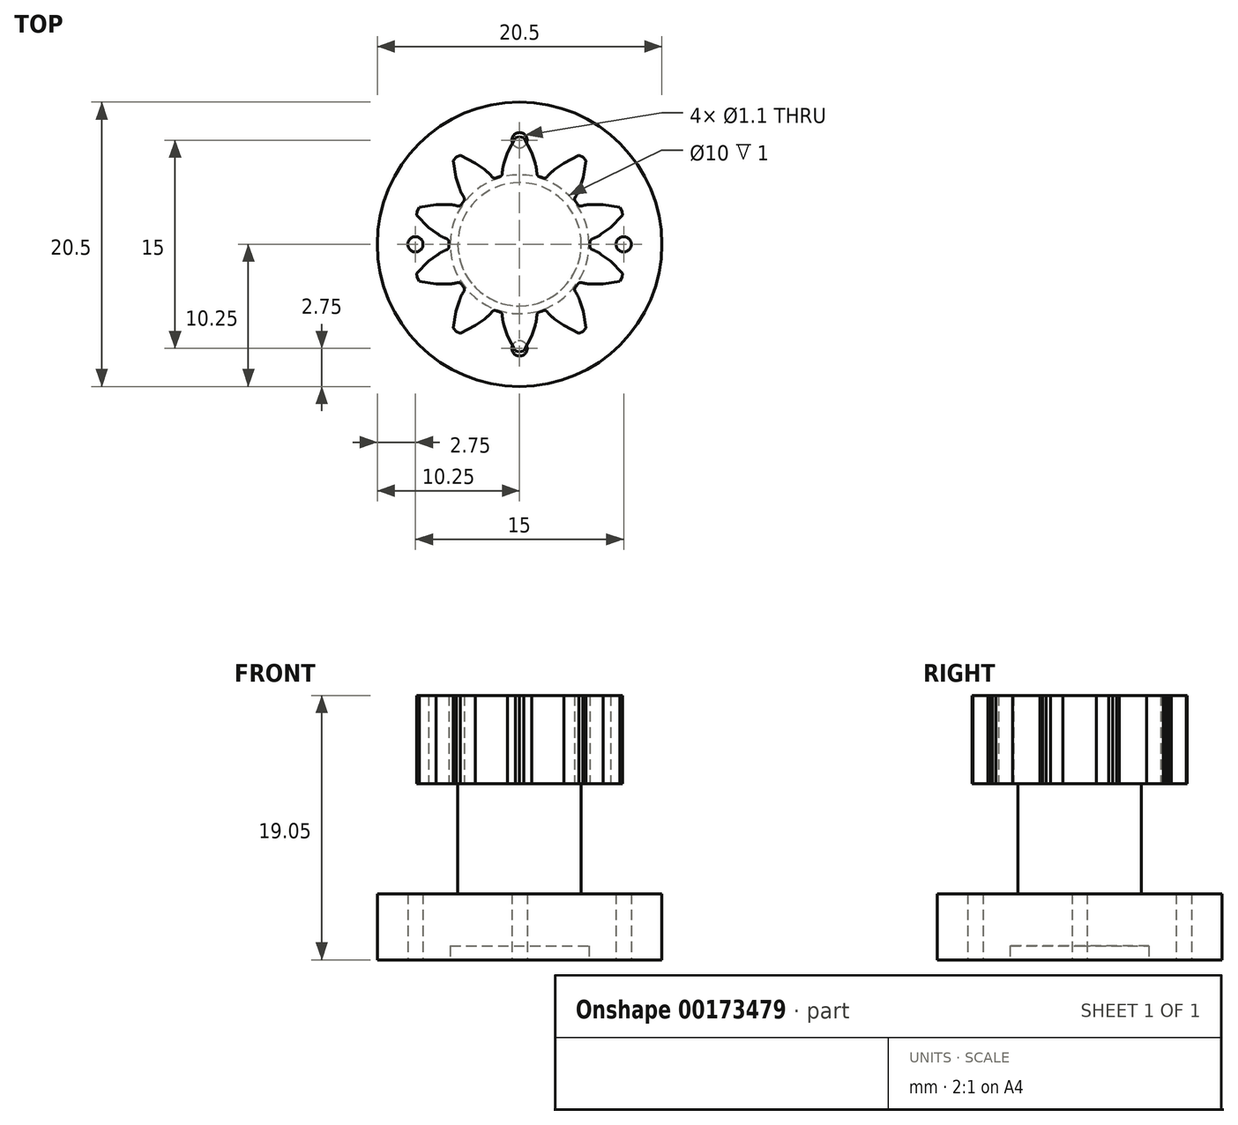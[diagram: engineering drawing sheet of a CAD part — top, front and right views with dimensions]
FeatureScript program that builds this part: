
annotation { "Feature Type Name" : "Feature", "Feature Type Description" : "" }
export const myFeature = defineFeature(function(context is Context, id is Id, definition is map)
    precondition{}
    {
        {
            var Q0;
            Q0=qCreatedBy(makeId("Top.planeOp"),FACE);
            var sketch = newSketch(context, id + "F0", { "sketchPlane" : qUnion([Q0])});
            skCircle(sketch, "E0", {"center": v(0, 0) * mm, "radius": 5.08 * mm});
            skLineSegment(sketch, "E1", {"start": v(0, 5.08) * mm, "end": v(0, 7.75) * mm, "construction": true});
            skLineSegment(sketch, "E2", {"start": v(0, 5.08) * mm, "end": v(-1.6, 5.08) * mm});
            skLineSegment(sketch, "E3", {"start": v(-1.24, 5.08) * mm, "end": v(-1.24, 5.46) * mm});
            skLineSegment(sketch, "E4", {"start": v(-0.86, 5.08) * mm, "end": v(-0.86, 6.6) * mm, "construction": true});
            skLineSegment(sketch, "E5", {"start": v(-0.3, 5.08) * mm, "end": v(-0.3, 7.7) * mm, "construction": true});
            skLineSegment(sketch, "E6", {"start": v(-0.3, 7.7) * mm, "end": v(0, 7.75) * mm});
            skLineSegment(sketch, "E7", {"start": v(-0.3, 7.7) * mm, "end": v(-0.86, 6.6) * mm});
            skLineSegment(sketch, "E8", {"start": v(-0.86, 6.6) * mm, "end": v(-1.24, 5.46) * mm});
            skLineSegment(sketch, "E9", {"start": v(-1.24, 5.08) * mm, "end": v(-1.24, 4.93) * mm});
            skLineSegment(sketch, "E10.MirrorCS", {"start": v(1.24, 5.08) * mm, "end": v(1.24, 4.93) * mm});
            skLineSegment(sketch, "E11.MirrorCS", {"start": v(0.86, 5.08) * mm, "end": v(0.86, 6.6) * mm, "construction": true});
            skLineSegment(sketch, "E12.MirrorCS", {"start": v(0.86, 6.6) * mm, "end": v(1.24, 5.46) * mm});
            skLineSegment(sketch, "E13.MirrorCS", {"start": v(0.3, 7.7) * mm, "end": v(0.86, 6.6) * mm});
            skLineSegment(sketch, "E14.MirrorCS", {"start": v(0.3, 5.08) * mm, "end": v(0.3, 7.7) * mm, "construction": true});
            skLineSegment(sketch, "E15.MirrorCS", {"start": v(0.3, 7.7) * mm, "end": v(0, 7.75) * mm});
            skLineSegment(sketch, "E16.MirrorCS", {"start": v(0, 5.08) * mm, "end": v(1.6, 5.08) * mm});
            skLineSegment(sketch, "E17.MirrorCS", {"start": v(1.24, 5.08) * mm, "end": v(1.24, 5.46) * mm});
            skLineSegment(sketch, "E18.1.0", {"start": v(-2.99, 4.1) * mm, "end": v(-1.7, 5.05) * mm});
            skLineSegment(sketch, "E18.1.1", {"start": v(-3.23, 3.93) * mm, "end": v(-4.77, 6.05) * mm, "construction": true});
            skLineSegment(sketch, "E18.1.2", {"start": v(-3.68, 3.6) * mm, "end": v(-4.58, 4.84) * mm, "construction": true});
            skLineSegment(sketch, "E18.1.3", {"start": v(-2.99, 4.1) * mm, "end": v(-4.28, 3.17) * mm});
            skLineSegment(sketch, "E18.1.4", {"start": v(-2.99, 4.1) * mm, "end": v(-4.56, 6.27) * mm, "construction": true});
            skLineSegment(sketch, "E18.1.5", {"start": v(-4.28, 6.4) * mm, "end": v(-3.18, 5.85) * mm});
            skLineSegment(sketch, "E18.1.6", {"start": v(-3.18, 5.85) * mm, "end": v(-2.2, 5.15) * mm});
            skLineSegment(sketch, "E18.1.7", {"start": v(-4.77, 6.05) * mm, "end": v(-4.56, 6.27) * mm});
            skLineSegment(sketch, "E18.1.8", {"start": v(-4, 3.38) * mm, "end": v(-4.22, 3.69) * mm});
            skLineSegment(sketch, "E18.1.9", {"start": v(-2.74, 4.29) * mm, "end": v(-4.28, 6.4) * mm, "construction": true});
            skLineSegment(sketch, "E18.1.10", {"start": v(-4.77, 6.05) * mm, "end": v(-4.58, 4.84) * mm});
            skLineSegment(sketch, "E18.1.11", {"start": v(-4.58, 4.84) * mm, "end": v(-4.22, 3.69) * mm});
            skLineSegment(sketch, "E18.1.12", {"start": v(-2.29, 4.62) * mm, "end": v(-3.18, 5.85) * mm, "construction": true});
            skLineSegment(sketch, "E18.1.13", {"start": v(-1.98, 4.84) * mm, "end": v(-2.2, 5.15) * mm});
            skLineSegment(sketch, "E18.1.14", {"start": v(-4.28, 6.4) * mm, "end": v(-4.56, 6.27) * mm});
            skLineSegment(sketch, "E18.1.15", {"start": v(-1.98, 4.84) * mm, "end": v(-1.89, 4.72) * mm});
            skLineSegment(sketch, "E18.1.16", {"start": v(-4, 3.38) * mm, "end": v(-3.9, 3.25) * mm});
            skLineSegment(sketch, "E18.2.0", {"start": v(-4.83, 1.57) * mm, "end": v(-4.34, 3.1) * mm});
            skLineSegment(sketch, "E18.2.1", {"start": v(-4.93, 1.28) * mm, "end": v(-7.41, 2.09) * mm, "construction": true});
            skLineSegment(sketch, "E18.2.2", {"start": v(-5.1, 0.75) * mm, "end": v(-6.55, 1.22) * mm, "construction": true});
            skLineSegment(sketch, "E18.2.3", {"start": v(-4.83, 1.57) * mm, "end": v(-5.33, 0.05) * mm});
            skLineSegment(sketch, "E18.2.4", {"start": v(-4.83, 1.57) * mm, "end": v(-7.37, 2.4) * mm, "construction": true});
            skLineSegment(sketch, "E18.2.5", {"start": v(-7.23, 2.67) * mm, "end": v(-6.01, 2.86) * mm});
            skLineSegment(sketch, "E18.2.6", {"start": v(-6.01, 2.86) * mm, "end": v(-4.8, 2.87) * mm});
            skLineSegment(sketch, "E18.2.7", {"start": v(-7.41, 2.09) * mm, "end": v(-7.37, 2.4) * mm});
            skLineSegment(sketch, "E18.2.8", {"start": v(-5.22, 0.39) * mm, "end": v(-5.58, 0.5) * mm});
            skLineSegment(sketch, "E18.2.9", {"start": v(-4.74, 1.86) * mm, "end": v(-7.23, 2.67) * mm, "construction": true});
            skLineSegment(sketch, "E18.2.10", {"start": v(-7.41, 2.09) * mm, "end": v(-6.55, 1.22) * mm});
            skLineSegment(sketch, "E18.2.11", {"start": v(-6.55, 1.22) * mm, "end": v(-5.58, 0.5) * mm});
            skLineSegment(sketch, "E18.2.12", {"start": v(-4.56, 2.4) * mm, "end": v(-6.01, 2.86) * mm, "construction": true});
            skLineSegment(sketch, "E18.2.13", {"start": v(-4.45, 2.75) * mm, "end": v(-4.8, 2.87) * mm});
            skLineSegment(sketch, "E18.2.14", {"start": v(-7.23, 2.67) * mm, "end": v(-7.37, 2.4) * mm});
            skLineSegment(sketch, "E18.2.15", {"start": v(-4.45, 2.75) * mm, "end": v(-4.3, 2.7) * mm});
            skLineSegment(sketch, "E18.2.16", {"start": v(-5.22, 0.39) * mm, "end": v(-5.07, 0.34) * mm});
            skLineSegment(sketch, "E18.3.0", {"start": v(-4.83, -1.57) * mm, "end": v(-5.33, -0.05) * mm});
            skLineSegment(sketch, "E18.3.1", {"start": v(-4.74, -1.86) * mm, "end": v(-7.23, -2.67) * mm, "construction": true});
            skLineSegment(sketch, "E18.3.2", {"start": v(-4.56, -2.4) * mm, "end": v(-6.01, -2.86) * mm, "construction": true});
            skLineSegment(sketch, "E18.3.3", {"start": v(-4.83, -1.57) * mm, "end": v(-4.34, -3.1) * mm});
            skLineSegment(sketch, "E18.3.4", {"start": v(-4.83, -1.57) * mm, "end": v(-7.37, -2.4) * mm, "construction": true});
            skLineSegment(sketch, "E18.3.5", {"start": v(-7.41, -2.09) * mm, "end": v(-6.55, -1.22) * mm});
            skLineSegment(sketch, "E18.3.6", {"start": v(-6.55, -1.22) * mm, "end": v(-5.58, -0.5) * mm});
            skLineSegment(sketch, "E18.3.7", {"start": v(-7.23, -2.67) * mm, "end": v(-7.37, -2.4) * mm});
            skLineSegment(sketch, "E18.3.8", {"start": v(-4.45, -2.75) * mm, "end": v(-4.8, -2.87) * mm});
            skLineSegment(sketch, "E18.3.9", {"start": v(-4.93, -1.28) * mm, "end": v(-7.41, -2.09) * mm, "construction": true});
            skLineSegment(sketch, "E18.3.10", {"start": v(-7.23, -2.67) * mm, "end": v(-6.01, -2.86) * mm});
            skLineSegment(sketch, "E18.3.11", {"start": v(-6.01, -2.86) * mm, "end": v(-4.8, -2.87) * mm});
            skLineSegment(sketch, "E18.3.12", {"start": v(-5.1, -0.75) * mm, "end": v(-6.55, -1.22) * mm, "construction": true});
            skLineSegment(sketch, "E18.3.13", {"start": v(-5.22, -0.39) * mm, "end": v(-5.58, -0.5) * mm});
            skLineSegment(sketch, "E18.3.14", {"start": v(-7.41, -2.09) * mm, "end": v(-7.37, -2.4) * mm});
            skLineSegment(sketch, "E18.3.15", {"start": v(-5.22, -0.39) * mm, "end": v(-5.07, -0.34) * mm});
            skLineSegment(sketch, "E18.3.16", {"start": v(-4.45, -2.75) * mm, "end": v(-4.3, -2.7) * mm});
            skLineSegment(sketch, "E18.4.0", {"start": v(-2.99, -4.1) * mm, "end": v(-4.28, -3.17) * mm});
            skLineSegment(sketch, "E18.4.1", {"start": v(-2.74, -4.29) * mm, "end": v(-4.28, -6.4) * mm, "construction": true});
            skLineSegment(sketch, "E18.4.2", {"start": v(-2.29, -4.62) * mm, "end": v(-3.18, -5.85) * mm, "construction": true});
            skLineSegment(sketch, "E18.4.3", {"start": v(-2.99, -4.1) * mm, "end": v(-1.7, -5.05) * mm});
            skLineSegment(sketch, "E18.4.4", {"start": v(-2.99, -4.1) * mm, "end": v(-4.56, -6.27) * mm, "construction": true});
            skLineSegment(sketch, "E18.4.5", {"start": v(-4.77, -6.05) * mm, "end": v(-4.58, -4.84) * mm});
            skLineSegment(sketch, "E18.4.6", {"start": v(-4.58, -4.84) * mm, "end": v(-4.22, -3.69) * mm});
            skLineSegment(sketch, "E18.4.7", {"start": v(-4.28, -6.4) * mm, "end": v(-4.56, -6.27) * mm});
            skLineSegment(sketch, "E18.4.8", {"start": v(-1.98, -4.84) * mm, "end": v(-2.2, -5.15) * mm});
            skLineSegment(sketch, "E18.4.9", {"start": v(-3.23, -3.93) * mm, "end": v(-4.77, -6.05) * mm, "construction": true});
            skLineSegment(sketch, "E18.4.10", {"start": v(-4.28, -6.4) * mm, "end": v(-3.18, -5.85) * mm});
            skLineSegment(sketch, "E18.4.11", {"start": v(-3.18, -5.85) * mm, "end": v(-2.2, -5.15) * mm});
            skLineSegment(sketch, "E18.4.12", {"start": v(-3.68, -3.6) * mm, "end": v(-4.58, -4.84) * mm, "construction": true});
            skLineSegment(sketch, "E18.4.13", {"start": v(-4, -3.38) * mm, "end": v(-4.22, -3.69) * mm});
            skLineSegment(sketch, "E18.4.14", {"start": v(-4.77, -6.05) * mm, "end": v(-4.56, -6.27) * mm});
            skLineSegment(sketch, "E18.4.15", {"start": v(-4, -3.38) * mm, "end": v(-3.9, -3.25) * mm});
            skLineSegment(sketch, "E18.4.16", {"start": v(-1.98, -4.84) * mm, "end": v(-1.89, -4.72) * mm});
            skLineSegment(sketch, "E18.5.0", {"start": v(0, -5.08) * mm, "end": v(-1.6, -5.08) * mm});
            skLineSegment(sketch, "E18.5.1", {"start": v(0.3, -5.08) * mm, "end": v(0.3, -7.7) * mm, "construction": true});
            skLineSegment(sketch, "E18.5.2", {"start": v(0.86, -5.08) * mm, "end": v(0.86, -6.6) * mm, "construction": true});
            skLineSegment(sketch, "E18.5.3", {"start": v(0, -5.08) * mm, "end": v(1.6, -5.08) * mm});
            skLineSegment(sketch, "E18.5.4", {"start": v(0, -5.08) * mm, "end": v(0, -7.75) * mm, "construction": true});
            skLineSegment(sketch, "E18.5.5", {"start": v(-0.3, -7.7) * mm, "end": v(-0.86, -6.6) * mm});
            skLineSegment(sketch, "E18.5.6", {"start": v(-0.86, -6.6) * mm, "end": v(-1.24, -5.46) * mm});
            skLineSegment(sketch, "E18.5.7", {"start": v(0.3, -7.7) * mm, "end": v(0, -7.75) * mm});
            skLineSegment(sketch, "E18.5.8", {"start": v(1.24, -5.08) * mm, "end": v(1.24, -5.46) * mm});
            skLineSegment(sketch, "E18.5.9", {"start": v(-0.3, -5.08) * mm, "end": v(-0.3, -7.7) * mm, "construction": true});
            skLineSegment(sketch, "E18.5.10", {"start": v(0.3, -7.7) * mm, "end": v(0.86, -6.6) * mm});
            skLineSegment(sketch, "E18.5.11", {"start": v(0.86, -6.6) * mm, "end": v(1.24, -5.46) * mm});
            skLineSegment(sketch, "E18.5.12", {"start": v(-0.86, -5.08) * mm, "end": v(-0.86, -6.6) * mm, "construction": true});
            skLineSegment(sketch, "E18.5.13", {"start": v(-1.24, -5.08) * mm, "end": v(-1.24, -5.46) * mm});
            skLineSegment(sketch, "E18.5.14", {"start": v(-0.3, -7.7) * mm, "end": v(0, -7.75) * mm});
            skLineSegment(sketch, "E18.5.15", {"start": v(-1.24, -5.08) * mm, "end": v(-1.24, -4.93) * mm});
            skLineSegment(sketch, "E18.5.16", {"start": v(1.24, -5.08) * mm, "end": v(1.24, -4.93) * mm});
            skLineSegment(sketch, "E18.6.0", {"start": v(2.99, -4.1) * mm, "end": v(1.7, -5.05) * mm});
            skLineSegment(sketch, "E18.6.1", {"start": v(3.23, -3.93) * mm, "end": v(4.77, -6.05) * mm, "construction": true});
            skLineSegment(sketch, "E18.6.2", {"start": v(3.68, -3.6) * mm, "end": v(4.58, -4.84) * mm, "construction": true});
            skLineSegment(sketch, "E18.6.3", {"start": v(2.99, -4.1) * mm, "end": v(4.28, -3.17) * mm});
            skLineSegment(sketch, "E18.6.4", {"start": v(2.99, -4.1) * mm, "end": v(4.56, -6.27) * mm, "construction": true});
            skLineSegment(sketch, "E18.6.5", {"start": v(4.28, -6.4) * mm, "end": v(3.18, -5.85) * mm});
            skLineSegment(sketch, "E18.6.6", {"start": v(3.18, -5.85) * mm, "end": v(2.2, -5.15) * mm});
            skLineSegment(sketch, "E18.6.7", {"start": v(4.77, -6.05) * mm, "end": v(4.56, -6.27) * mm});
            skLineSegment(sketch, "E18.6.8", {"start": v(4, -3.38) * mm, "end": v(4.22, -3.69) * mm});
            skLineSegment(sketch, "E18.6.9", {"start": v(2.74, -4.29) * mm, "end": v(4.28, -6.4) * mm, "construction": true});
            skLineSegment(sketch, "E18.6.10", {"start": v(4.77, -6.05) * mm, "end": v(4.58, -4.84) * mm});
            skLineSegment(sketch, "E18.6.11", {"start": v(4.58, -4.84) * mm, "end": v(4.22, -3.69) * mm});
            skLineSegment(sketch, "E18.6.12", {"start": v(2.29, -4.62) * mm, "end": v(3.18, -5.85) * mm, "construction": true});
            skLineSegment(sketch, "E18.6.13", {"start": v(1.98, -4.84) * mm, "end": v(2.2, -5.15) * mm});
            skLineSegment(sketch, "E18.6.14", {"start": v(4.28, -6.4) * mm, "end": v(4.56, -6.27) * mm});
            skLineSegment(sketch, "E18.6.15", {"start": v(1.98, -4.84) * mm, "end": v(1.89, -4.72) * mm});
            skLineSegment(sketch, "E18.6.16", {"start": v(4, -3.38) * mm, "end": v(3.9, -3.25) * mm});
            skLineSegment(sketch, "E18.7.0", {"start": v(4.83, -1.57) * mm, "end": v(4.34, -3.1) * mm});
            skLineSegment(sketch, "E18.7.1", {"start": v(4.93, -1.28) * mm, "end": v(7.41, -2.09) * mm, "construction": true});
            skLineSegment(sketch, "E18.7.2", {"start": v(5.1, -0.75) * mm, "end": v(6.55, -1.22) * mm, "construction": true});
            skLineSegment(sketch, "E18.7.3", {"start": v(4.83, -1.57) * mm, "end": v(5.33, -0.05) * mm});
            skLineSegment(sketch, "E18.7.4", {"start": v(4.83, -1.57) * mm, "end": v(7.37, -2.4) * mm, "construction": true});
            skLineSegment(sketch, "E18.7.5", {"start": v(7.23, -2.67) * mm, "end": v(6.01, -2.86) * mm});
            skLineSegment(sketch, "E18.7.6", {"start": v(6.01, -2.86) * mm, "end": v(4.8, -2.87) * mm});
            skLineSegment(sketch, "E18.7.7", {"start": v(7.41, -2.09) * mm, "end": v(7.37, -2.4) * mm});
            skLineSegment(sketch, "E18.7.8", {"start": v(5.22, -0.39) * mm, "end": v(5.58, -0.5) * mm});
            skLineSegment(sketch, "E18.7.9", {"start": v(4.74, -1.86) * mm, "end": v(7.23, -2.67) * mm, "construction": true});
            skLineSegment(sketch, "E18.7.10", {"start": v(7.41, -2.09) * mm, "end": v(6.55, -1.22) * mm});
            skLineSegment(sketch, "E18.7.11", {"start": v(6.55, -1.22) * mm, "end": v(5.58, -0.5) * mm});
            skLineSegment(sketch, "E18.7.12", {"start": v(4.56, -2.4) * mm, "end": v(6.01, -2.86) * mm, "construction": true});
            skLineSegment(sketch, "E18.7.13", {"start": v(4.45, -2.75) * mm, "end": v(4.8, -2.87) * mm});
            skLineSegment(sketch, "E18.7.14", {"start": v(7.23, -2.67) * mm, "end": v(7.37, -2.4) * mm});
            skLineSegment(sketch, "E18.7.15", {"start": v(4.45, -2.75) * mm, "end": v(4.3, -2.7) * mm});
            skLineSegment(sketch, "E18.7.16", {"start": v(5.22, -0.39) * mm, "end": v(5.07, -0.34) * mm});
            skLineSegment(sketch, "E19.3.8.0", {"start": v(4.74, 1.86) * mm, "end": v(7.23, 2.67) * mm, "construction": true});
            skLineSegment(sketch, "E19.6.8.0", {"start": v(4.56, 2.4) * mm, "end": v(6.01, 2.86) * mm, "construction": true});
            skLineSegment(sketch, "E19.9.8.0", {"start": v(4.83, 1.57) * mm, "end": v(4.34, 3.1) * mm});
            skLineSegment(sketch, "E19.11.8.0", {"start": v(4.83, 1.57) * mm, "end": v(5.33, 0.05) * mm});
            skLineSegment(sketch, "E19.12.8.0", {"start": v(4.83, 1.57) * mm, "end": v(7.37, 2.4) * mm, "construction": true});
            skLineSegment(sketch, "E19.15.8.0", {"start": v(7.41, 2.09) * mm, "end": v(6.55, 1.22) * mm});
            skLineSegment(sketch, "E19.18.8.0", {"start": v(6.55, 1.22) * mm, "end": v(5.58, 0.5) * mm});
            skLineSegment(sketch, "E19.21.8.0", {"start": v(7.23, 2.67) * mm, "end": v(7.37, 2.4) * mm});
            skLineSegment(sketch, "E19.24.8.0", {"start": v(4.45, 2.75) * mm, "end": v(4.8, 2.87) * mm});
            skLineSegment(sketch, "E19.27.8.0", {"start": v(4.93, 1.28) * mm, "end": v(7.41, 2.09) * mm, "construction": true});
            skLineSegment(sketch, "E19.30.8.0", {"start": v(7.23, 2.67) * mm, "end": v(6.01, 2.86) * mm});
            skLineSegment(sketch, "E19.33.8.0", {"start": v(6.01, 2.86) * mm, "end": v(4.8, 2.87) * mm});
            skLineSegment(sketch, "E19.36.8.0", {"start": v(5.1, 0.75) * mm, "end": v(6.55, 1.22) * mm, "construction": true});
            skLineSegment(sketch, "E19.39.8.0", {"start": v(5.22, 0.39) * mm, "end": v(5.58, 0.5) * mm});
            skLineSegment(sketch, "E19.42.8.0", {"start": v(7.41, 2.09) * mm, "end": v(7.37, 2.4) * mm});
            skLineSegment(sketch, "E19.45.8.0", {"start": v(5.22, 0.39) * mm, "end": v(5.07, 0.34) * mm});
            skLineSegment(sketch, "E19.48.8.0", {"start": v(4.45, 2.75) * mm, "end": v(4.3, 2.7) * mm});
            skLineSegment(sketch, "E19.3.9.0", {"start": v(2.74, 4.29) * mm, "end": v(4.28, 6.4) * mm, "construction": true});
            skLineSegment(sketch, "E19.6.9.0", {"start": v(2.29, 4.62) * mm, "end": v(3.18, 5.85) * mm, "construction": true});
            skLineSegment(sketch, "E19.9.9.0", {"start": v(2.99, 4.1) * mm, "end": v(1.7, 5.05) * mm});
            skLineSegment(sketch, "E19.11.9.0", {"start": v(2.99, 4.1) * mm, "end": v(4.28, 3.17) * mm});
            skLineSegment(sketch, "E19.12.9.0", {"start": v(2.99, 4.1) * mm, "end": v(4.56, 6.27) * mm, "construction": true});
            skLineSegment(sketch, "E19.15.9.0", {"start": v(4.77, 6.05) * mm, "end": v(4.58, 4.84) * mm});
            skLineSegment(sketch, "E19.18.9.0", {"start": v(4.58, 4.84) * mm, "end": v(4.22, 3.69) * mm});
            skLineSegment(sketch, "E19.21.9.0", {"start": v(4.28, 6.4) * mm, "end": v(4.56, 6.27) * mm});
            skLineSegment(sketch, "E19.24.9.0", {"start": v(1.98, 4.84) * mm, "end": v(2.2, 5.15) * mm});
            skLineSegment(sketch, "E19.27.9.0", {"start": v(3.23, 3.93) * mm, "end": v(4.77, 6.05) * mm, "construction": true});
            skLineSegment(sketch, "E19.30.9.0", {"start": v(4.28, 6.4) * mm, "end": v(3.18, 5.85) * mm});
            skLineSegment(sketch, "E19.33.9.0", {"start": v(3.18, 5.85) * mm, "end": v(2.2, 5.15) * mm});
            skLineSegment(sketch, "E19.36.9.0", {"start": v(3.68, 3.6) * mm, "end": v(4.58, 4.84) * mm, "construction": true});
            skLineSegment(sketch, "E19.39.9.0", {"start": v(4, 3.38) * mm, "end": v(4.22, 3.69) * mm});
            skLineSegment(sketch, "E19.42.9.0", {"start": v(4.77, 6.05) * mm, "end": v(4.56, 6.27) * mm});
            skLineSegment(sketch, "E19.45.9.0", {"start": v(4, 3.38) * mm, "end": v(3.9, 3.25) * mm});
            skLineSegment(sketch, "E19.48.9.0", {"start": v(1.98, 4.84) * mm, "end": v(1.89, 4.72) * mm});
            skSolve(sketch);
        }
        {
            var Q0;
            Q0 = qSketchRegion(id + "F0", true);
            extrude(context, id + "F1", {"entities" : qUnion([Q0]), "depth" : 6.35 * mm});
        }
        {
            var Q0;
            Q0=makeQuery(id+"F1.opExtrude","SWEPT_EDGE",EDGE,{"disambiguationData":[OSD([sQuery(id+"F0.wireOp",EDGE,"E0"),sQuery(id+"F0.wireOp",EDGE,"E18.9.16")])]});
            var Q1;
            Q1=makeQuery(id+"F1.opExtrude","SWEPT_EDGE",EDGE,{"disambiguationData":[OSD([sQuery(id+"F0.wireOp",EDGE,"E0"),sQuery(id+"F0.wireOp",EDGE,"E18.10.15")])]});
            var Q2;
            Q2=makeQuery(id+"F1.opExtrude","SWEPT_EDGE",EDGE,{"disambiguationData":[OSD([sQuery(id+"F0.wireOp",EDGE,"E0"),sQuery(id+"F0.wireOp",EDGE,"E18.11.15")])]});
            var Q3;
            Q3=makeQuery(id+"F1.opExtrude","SWEPT_EDGE",EDGE,{"disambiguationData":[OSD([sQuery(id+"F0.wireOp",EDGE,"E0"),sQuery(id+"F0.wireOp",EDGE,"E18.10.16")])]});
            var Q4;
            Q4=makeQuery(id+"F1.opExtrude","SWEPT_EDGE",EDGE,{"disambiguationData":[OSD([sQuery(id+"F0.wireOp",EDGE,"E0"),sQuery(id+"F0.wireOp",EDGE,"E10.MirrorCS")])]});
            var Q5;
            Q5=makeQuery(id+"F1.opExtrude","SWEPT_EDGE",EDGE,{"disambiguationData":[OSD([sQuery(id+"F0.wireOp",EDGE,"E0"),sQuery(id+"F0.wireOp",EDGE,"E18.11.16")])]});
            var Q6;
            Q6=makeQuery(id+"F1.opExtrude","SWEPT_EDGE",EDGE,{"disambiguationData":[OSD([sQuery(id+"F0.wireOp",EDGE,"E0"),sQuery(id+"F0.wireOp",EDGE,"E18.1.15")])]});
            var Q7;
            Q7=makeQuery(id+"F1.opExtrude","SWEPT_EDGE",EDGE,{"disambiguationData":[OSD([sQuery(id+"F0.wireOp",EDGE,"E0"),sQuery(id+"F0.wireOp",EDGE,"E9")])]});
            var Q8;
            Q8=makeQuery(id+"F1.opExtrude","SWEPT_EDGE",EDGE,{"disambiguationData":[OSD([sQuery(id+"F0.wireOp",EDGE,"E0"),sQuery(id+"F0.wireOp",EDGE,"E18.1.16")])]});
            var Q9;
            Q9=makeQuery(id+"F1.opExtrude","SWEPT_EDGE",EDGE,{"disambiguationData":[OSD([sQuery(id+"F0.wireOp",EDGE,"E0"),sQuery(id+"F0.wireOp",EDGE,"E18.2.15")])]});
            var Q10;
            Q10=makeQuery(id+"F1.opExtrude","SWEPT_EDGE",EDGE,{"disambiguationData":[OSD([sQuery(id+"F0.wireOp",EDGE,"E0"),sQuery(id+"F0.wireOp",EDGE,"E18.2.16")])]});
            var Q11;
            Q11=makeQuery(id+"F1.opExtrude","SWEPT_EDGE",EDGE,{"disambiguationData":[OSD([sQuery(id+"F0.wireOp",EDGE,"E0"),sQuery(id+"F0.wireOp",EDGE,"E18.3.15")])]});
            var Q12;
            Q12=makeQuery(id+"F1.opExtrude","SWEPT_EDGE",EDGE,{"disambiguationData":[OSD([sQuery(id+"F0.wireOp",EDGE,"E0"),sQuery(id+"F0.wireOp",EDGE,"E18.3.16")])]});
            var Q13;
            Q13=makeQuery(id+"F1.opExtrude","SWEPT_EDGE",EDGE,{"disambiguationData":[OSD([sQuery(id+"F0.wireOp",EDGE,"E0"),sQuery(id+"F0.wireOp",EDGE,"E18.4.15")])]});
            var Q14;
            Q14=makeQuery(id+"F1.opExtrude","SWEPT_EDGE",EDGE,{"disambiguationData":[OSD([sQuery(id+"F0.wireOp",EDGE,"E0"),sQuery(id+"F0.wireOp",EDGE,"E18.4.16")])]});
            var Q15;
            Q15=makeQuery(id+"F1.opExtrude","SWEPT_EDGE",EDGE,{"disambiguationData":[OSD([sQuery(id+"F0.wireOp",EDGE,"E0"),sQuery(id+"F0.wireOp",EDGE,"E18.5.15")])]});
            var Q16;
            Q16=makeQuery(id+"F1.opExtrude","SWEPT_EDGE",EDGE,{"disambiguationData":[OSD([sQuery(id+"F0.wireOp",EDGE,"E0"),sQuery(id+"F0.wireOp",EDGE,"E18.5.16")])]});
            var Q17;
            Q17=makeQuery(id+"F1.opExtrude","SWEPT_EDGE",EDGE,{"disambiguationData":[OSD([sQuery(id+"F0.wireOp",EDGE,"E0"),sQuery(id+"F0.wireOp",EDGE,"E18.6.15")])]});
            var Q18;
            Q18=makeQuery(id+"F1.opExtrude","SWEPT_EDGE",EDGE,{"disambiguationData":[OSD([sQuery(id+"F0.wireOp",EDGE,"E0"),sQuery(id+"F0.wireOp",EDGE,"E18.6.16")])]});
            var Q19;
            Q19=makeQuery(id+"F1.opExtrude","SWEPT_EDGE",EDGE,{"disambiguationData":[OSD([sQuery(id+"F0.wireOp",EDGE,"E0"),sQuery(id+"F0.wireOp",EDGE,"E18.7.15")])]});
            var Q20;
            Q20=makeQuery(id+"F1.opExtrude","SWEPT_EDGE",EDGE,{"disambiguationData":[OSD([sQuery(id+"F0.wireOp",EDGE,"E0"),sQuery(id+"F0.wireOp",EDGE,"E18.7.16")])]});
            var Q21;
            Q21=makeQuery(id+"F1.opExtrude","SWEPT_EDGE",EDGE,{"disambiguationData":[OSD([sQuery(id+"F0.wireOp",EDGE,"E0"),sQuery(id+"F0.wireOp",EDGE,"E18.8.15")])]});
            var Q22;
            Q22=makeQuery(id+"F1.opExtrude","SWEPT_EDGE",EDGE,{"disambiguationData":[OSD([sQuery(id+"F0.wireOp",EDGE,"E0"),sQuery(id+"F0.wireOp",EDGE,"E18.9.15")])]});
            var Q23;
            Q23=makeQuery(id+"F1.opExtrude","SWEPT_EDGE",EDGE,{"disambiguationData":[OSD([sQuery(id+"F0.wireOp",EDGE,"E0"),sQuery(id+"F0.wireOp",EDGE,"E18.8.16")])]});
            fillet(context, id + "F2", {"entities" : qUnion([Q0, Q1, Q2, Q3, Q4, Q5, Q6, Q7, Q8, Q9, Q10, Q11, Q12, Q13, Q14, Q15, Q16, Q17, Q18, Q19, Q20, Q21, Q22, Q23]), "radius" : 0.25 * mm, "tangentPropagation" : true, "allowEdgeOverflow" : false});
        }
        {
            var Q0;
            Q0=makeQuery(id+"F1.opExtrude","SWEPT_EDGE",EDGE,{"disambiguationData":[OSD([sQuery(id+"F0.wireOp",EDGE,"E18.10.6"),sQuery(id+"F0.wireOp",EDGE,"E18.10.13")])]});
            var Q1;
            Q1=makeQuery(id+"F1.opExtrude","SWEPT_EDGE",EDGE,{"disambiguationData":[OSD([sQuery(id+"F0.wireOp",EDGE,"E18.9.8"),sQuery(id+"F0.wireOp",EDGE,"E18.9.11")])]});
            var Q2;
            Q2=makeQuery(id+"F1.opExtrude","SWEPT_EDGE",EDGE,{"disambiguationData":[OSD([sQuery(id+"F0.wireOp",EDGE,"E18.10.8"),sQuery(id+"F0.wireOp",EDGE,"E18.10.11")])]});
            var Q3;
            Q3=makeQuery(id+"F1.opExtrude","SWEPT_EDGE",EDGE,{"disambiguationData":[OSD([sQuery(id+"F0.wireOp",EDGE,"E18.11.6"),sQuery(id+"F0.wireOp",EDGE,"E18.11.13")])]});
            var Q4;
            Q4=makeQuery(id+"F1.opExtrude","SWEPT_EDGE",EDGE,{"disambiguationData":[OSD([sQuery(id+"F0.wireOp",EDGE,"E12.MirrorCS"),sQuery(id+"F0.wireOp",EDGE,"E17.MirrorCS")])]});
            var Q5;
            Q5=makeQuery(id+"F1.opExtrude","SWEPT_EDGE",EDGE,{"disambiguationData":[OSD([sQuery(id+"F0.wireOp",EDGE,"E18.11.8"),sQuery(id+"F0.wireOp",EDGE,"E18.11.11")])]});
            var Q6;
            Q6=makeQuery(id+"F1.opExtrude","SWEPT_EDGE",EDGE,{"disambiguationData":[OSD([sQuery(id+"F0.wireOp",EDGE,"E3"),sQuery(id+"F0.wireOp",EDGE,"E8")])]});
            var Q7;
            Q7=makeQuery(id+"F1.opExtrude","SWEPT_EDGE",EDGE,{"disambiguationData":[OSD([sQuery(id+"F0.wireOp",EDGE,"E18.1.6"),sQuery(id+"F0.wireOp",EDGE,"E18.1.13")])]});
            var Q8;
            Q8=makeQuery(id+"F1.opExtrude","SWEPT_EDGE",EDGE,{"disambiguationData":[OSD([sQuery(id+"F0.wireOp",EDGE,"E18.2.6"),sQuery(id+"F0.wireOp",EDGE,"E18.2.13")])]});
            var Q9;
            Q9=makeQuery(id+"F1.opExtrude","SWEPT_EDGE",EDGE,{"disambiguationData":[OSD([sQuery(id+"F0.wireOp",EDGE,"E18.1.8"),sQuery(id+"F0.wireOp",EDGE,"E18.1.11")])]});
            var Q10;
            Q10=makeQuery(id+"F1.opExtrude","SWEPT_EDGE",EDGE,{"disambiguationData":[OSD([sQuery(id+"F0.wireOp",EDGE,"E18.2.8"),sQuery(id+"F0.wireOp",EDGE,"E18.2.11")])]});
            var Q11;
            Q11=makeQuery(id+"F1.opExtrude","SWEPT_EDGE",EDGE,{"disambiguationData":[OSD([sQuery(id+"F0.wireOp",EDGE,"E18.3.6"),sQuery(id+"F0.wireOp",EDGE,"E18.3.13")])]});
            var Q12;
            Q12=makeQuery(id+"F1.opExtrude","SWEPT_EDGE",EDGE,{"disambiguationData":[OSD([sQuery(id+"F0.wireOp",EDGE,"E18.3.8"),sQuery(id+"F0.wireOp",EDGE,"E18.3.11")])]});
            var Q13;
            Q13=makeQuery(id+"F1.opExtrude","SWEPT_EDGE",EDGE,{"disambiguationData":[OSD([sQuery(id+"F0.wireOp",EDGE,"E18.4.6"),sQuery(id+"F0.wireOp",EDGE,"E18.4.13")])]});
            var Q14;
            Q14=makeQuery(id+"F1.opExtrude","SWEPT_EDGE",EDGE,{"disambiguationData":[OSD([sQuery(id+"F0.wireOp",EDGE,"E18.4.8"),sQuery(id+"F0.wireOp",EDGE,"E18.4.11")])]});
            var Q15;
            Q15=makeQuery(id+"F1.opExtrude","SWEPT_EDGE",EDGE,{"disambiguationData":[OSD([sQuery(id+"F0.wireOp",EDGE,"E18.5.6"),sQuery(id+"F0.wireOp",EDGE,"E18.5.13")])]});
            var Q16;
            Q16=makeQuery(id+"F1.opExtrude","SWEPT_EDGE",EDGE,{"disambiguationData":[OSD([sQuery(id+"F0.wireOp",EDGE,"E18.5.8"),sQuery(id+"F0.wireOp",EDGE,"E18.5.11")])]});
            var Q17;
            Q17=makeQuery(id+"F1.opExtrude","SWEPT_EDGE",EDGE,{"disambiguationData":[OSD([sQuery(id+"F0.wireOp",EDGE,"E18.6.6"),sQuery(id+"F0.wireOp",EDGE,"E18.6.13")])]});
            var Q18;
            Q18=makeQuery(id+"F1.opExtrude","SWEPT_EDGE",EDGE,{"disambiguationData":[OSD([sQuery(id+"F0.wireOp",EDGE,"E18.7.6"),sQuery(id+"F0.wireOp",EDGE,"E18.7.13")])]});
            var Q19;
            Q19=makeQuery(id+"F1.opExtrude","SWEPT_EDGE",EDGE,{"disambiguationData":[OSD([sQuery(id+"F0.wireOp",EDGE,"E18.6.8"),sQuery(id+"F0.wireOp",EDGE,"E18.6.11")])]});
            var Q20;
            Q20=makeQuery(id+"F1.opExtrude","SWEPT_EDGE",EDGE,{"disambiguationData":[OSD([sQuery(id+"F0.wireOp",EDGE,"E18.8.6"),sQuery(id+"F0.wireOp",EDGE,"E18.8.13")])]});
            var Q21;
            Q21=makeQuery(id+"F1.opExtrude","SWEPT_EDGE",EDGE,{"disambiguationData":[OSD([sQuery(id+"F0.wireOp",EDGE,"E18.7.8"),sQuery(id+"F0.wireOp",EDGE,"E18.7.11")])]});
            var Q22;
            Q22=makeQuery(id+"F1.opExtrude","SWEPT_EDGE",EDGE,{"disambiguationData":[OSD([sQuery(id+"F0.wireOp",EDGE,"E18.8.8"),sQuery(id+"F0.wireOp",EDGE,"E18.8.11")])]});
            var Q23;
            Q23=makeQuery(id+"F1.opExtrude","SWEPT_EDGE",EDGE,{"disambiguationData":[OSD([sQuery(id+"F0.wireOp",EDGE,"E18.9.6"),sQuery(id+"F0.wireOp",EDGE,"E18.9.13")])]});
            var Q24;
            Q24=makeQuery(id+"F1.opExtrude","SWEPT_EDGE",EDGE,{"disambiguationData":[OSD([sQuery(id+"F0.wireOp",EDGE,"E19.18.9.0"),sQuery(id+"F0.wireOp",EDGE,"E19.39.9.0")])]});
            var Q25;
            Q25=makeQuery(id+"F1.opExtrude","SWEPT_EDGE",EDGE,{"disambiguationData":[OSD([sQuery(id+"F0.wireOp",EDGE,"E19.24.9.0"),sQuery(id+"F0.wireOp",EDGE,"E19.33.9.0")])]});
            var Q26;
            Q26=makeQuery(id+"F1.opExtrude","SWEPT_EDGE",EDGE,{"disambiguationData":[OSD([sQuery(id+"F0.wireOp",EDGE,"E19.24.8.0"),sQuery(id+"F0.wireOp",EDGE,"E19.33.8.0")])]});
            var Q27;
            Q27=makeQuery(id+"F1.opExtrude","SWEPT_EDGE",EDGE,{"disambiguationData":[OSD([sQuery(id+"F0.wireOp",EDGE,"E19.18.8.0"),sQuery(id+"F0.wireOp",EDGE,"E19.39.8.0")])]});
            fillet(context, id + "F3", {"entities" : qUnion([Q0, Q1, Q2, Q3, Q4, Q5, Q6, Q7, Q8, Q9, Q10, Q11, Q12, Q13, Q14, Q15, Q16, Q17, Q18, Q19, Q20, Q21, Q22, Q23, Q24, Q25, Q26, Q27]), "radius" : 2.54 * mm, "tangentPropagation" : true, "allowEdgeOverflow" : false});
        }
        {
            var Q0;
            Q0=makeQuery(id+"F1.opExtrude","CAP_FACE",FACE,{"disambiguationData":[OSD([sQuery(id+"F0.wireOp",EDGE,"E0"),sQuery(id+"F0.wireOp",EDGE,"E3"),sQuery(id+"F0.wireOp",EDGE,"E6"),sQuery(id+"F0.wireOp",EDGE,"E7"),sQuery(id+"F0.wireOp",EDGE,"E8"),sQuery(id+"F0.wireOp",EDGE,"E9"),sQuery(id+"F0.wireOp",EDGE,"E10.MirrorCS"),sQuery(id+"F0.wireOp",EDGE,"E12.MirrorCS"),sQuery(id+"F0.wireOp",EDGE,"E13.MirrorCS"),sQuery(id+"F0.wireOp",EDGE,"E15.MirrorCS"),sQuery(id+"F0.wireOp",EDGE,"E17.MirrorCS"),sQuery(id+"F0.wireOp",EDGE,"E18.1.5"),sQuery(id+"F0.wireOp",EDGE,"E18.1.6"),sQuery(id+"F0.wireOp",EDGE,"E18.1.7"),sQuery(id+"F0.wireOp",EDGE,"E18.1.8"),sQuery(id+"F0.wireOp",EDGE,"E18.1.10"),sQuery(id+"F0.wireOp",EDGE,"E18.1.11"),sQuery(id+"F0.wireOp",EDGE,"E18.1.13"),sQuery(id+"F0.wireOp",EDGE,"E18.1.14"),sQuery(id+"F0.wireOp",EDGE,"E18.1.15"),sQuery(id+"F0.wireOp",EDGE,"E18.1.16"),sQuery(id+"F0.wireOp",EDGE,"E18.2.5"),sQuery(id+"F0.wireOp",EDGE,"E18.2.6"),sQuery(id+"F0.wireOp",EDGE,"E18.2.7"),sQuery(id+"F0.wireOp",EDGE,"E18.2.8"),sQuery(id+"F0.wireOp",EDGE,"E18.2.10"),sQuery(id+"F0.wireOp",EDGE,"E18.2.11"),sQuery(id+"F0.wireOp",EDGE,"E18.2.13"),sQuery(id+"F0.wireOp",EDGE,"E18.2.14"),sQuery(id+"F0.wireOp",EDGE,"E18.2.15"),sQuery(id+"F0.wireOp",EDGE,"E18.2.16"),sQuery(id+"F0.wireOp",EDGE,"E18.3.5"),sQuery(id+"F0.wireOp",EDGE,"E18.3.6"),sQuery(id+"F0.wireOp",EDGE,"E18.3.7"),sQuery(id+"F0.wireOp",EDGE,"E18.3.8"),sQuery(id+"F0.wireOp",EDGE,"E18.3.10"),sQuery(id+"F0.wireOp",EDGE,"E18.3.11"),sQuery(id+"F0.wireOp",EDGE,"E18.3.13"),sQuery(id+"F0.wireOp",EDGE,"E18.3.14"),sQuery(id+"F0.wireOp",EDGE,"E18.3.15"),sQuery(id+"F0.wireOp",EDGE,"E18.3.16"),sQuery(id+"F0.wireOp",EDGE,"E18.4.5"),sQuery(id+"F0.wireOp",EDGE,"E18.4.6"),sQuery(id+"F0.wireOp",EDGE,"E18.4.7"),sQuery(id+"F0.wireOp",EDGE,"E18.4.8"),sQuery(id+"F0.wireOp",EDGE,"E18.4.10"),sQuery(id+"F0.wireOp",EDGE,"E18.4.11"),sQuery(id+"F0.wireOp",EDGE,"E18.4.13"),sQuery(id+"F0.wireOp",EDGE,"E18.4.14"),sQuery(id+"F0.wireOp",EDGE,"E18.4.15"),sQuery(id+"F0.wireOp",EDGE,"E18.4.16"),sQuery(id+"F0.wireOp",EDGE,"E18.5.5"),sQuery(id+"F0.wireOp",EDGE,"E18.5.6"),sQuery(id+"F0.wireOp",EDGE,"E18.5.7"),sQuery(id+"F0.wireOp",EDGE,"E18.5.8"),sQuery(id+"F0.wireOp",EDGE,"E18.5.10"),sQuery(id+"F0.wireOp",EDGE,"E18.5.11"),sQuery(id+"F0.wireOp",EDGE,"E18.5.13"),sQuery(id+"F0.wireOp",EDGE,"E18.5.14"),sQuery(id+"F0.wireOp",EDGE,"E18.5.15"),sQuery(id+"F0.wireOp",EDGE,"E18.5.16"),sQuery(id+"F0.wireOp",EDGE,"E18.6.5"),sQuery(id+"F0.wireOp",EDGE,"E18.6.6"),sQuery(id+"F0.wireOp",EDGE,"E18.6.7"),sQuery(id+"F0.wireOp",EDGE,"E18.6.8"),sQuery(id+"F0.wireOp",EDGE,"E18.6.10"),sQuery(id+"F0.wireOp",EDGE,"E18.6.11"),sQuery(id+"F0.wireOp",EDGE,"E18.6.13"),sQuery(id+"F0.wireOp",EDGE,"E18.6.14"),sQuery(id+"F0.wireOp",EDGE,"E18.6.15"),sQuery(id+"F0.wireOp",EDGE,"E18.6.16"),sQuery(id+"F0.wireOp",EDGE,"E18.7.5"),sQuery(id+"F0.wireOp",EDGE,"E18.7.6"),sQuery(id+"F0.wireOp",EDGE,"E18.7.7"),sQuery(id+"F0.wireOp",EDGE,"E18.7.8"),sQuery(id+"F0.wireOp",EDGE,"E18.7.10"),sQuery(id+"F0.wireOp",EDGE,"E18.7.11"),sQuery(id+"F0.wireOp",EDGE,"E18.7.13"),sQuery(id+"F0.wireOp",EDGE,"E18.7.14"),sQuery(id+"F0.wireOp",EDGE,"E18.7.15"),sQuery(id+"F0.wireOp",EDGE,"E18.7.16"),sQuery(id+"F0.wireOp",EDGE,"E18.8.5"),sQuery(id+"F0.wireOp",EDGE,"E18.8.6"),sQuery(id+"F0.wireOp",EDGE,"E18.8.7"),sQuery(id+"F0.wireOp",EDGE,"E18.8.8"),sQuery(id+"F0.wireOp",EDGE,"E18.8.10"),sQuery(id+"F0.wireOp",EDGE,"E18.8.11"),sQuery(id+"F0.wireOp",EDGE,"E18.8.13"),sQuery(id+"F0.wireOp",EDGE,"E18.8.14"),sQuery(id+"F0.wireOp",EDGE,"E18.8.15"),sQuery(id+"F0.wireOp",EDGE,"E18.8.16"),sQuery(id+"F0.wireOp",EDGE,"E18.9.5"),sQuery(id+"F0.wireOp",EDGE,"E18.9.6"),sQuery(id+"F0.wireOp",EDGE,"E18.9.7"),sQuery(id+"F0.wireOp",EDGE,"E18.9.8"),sQuery(id+"F0.wireOp",EDGE,"E18.9.10"),sQuery(id+"F0.wireOp",EDGE,"E18.9.11"),sQuery(id+"F0.wireOp",EDGE,"E18.9.13"),sQuery(id+"F0.wireOp",EDGE,"E18.9.14"),sQuery(id+"F0.wireOp",EDGE,"E18.9.15"),sQuery(id+"F0.wireOp",EDGE,"E18.9.16"),sQuery(id+"F0.wireOp",EDGE,"E18.10.5"),sQuery(id+"F0.wireOp",EDGE,"E18.10.6"),sQuery(id+"F0.wireOp",EDGE,"E18.10.7"),sQuery(id+"F0.wireOp",EDGE,"E18.10.8"),sQuery(id+"F0.wireOp",EDGE,"E18.10.10"),sQuery(id+"F0.wireOp",EDGE,"E18.10.11"),sQuery(id+"F0.wireOp",EDGE,"E18.10.13"),sQuery(id+"F0.wireOp",EDGE,"E18.10.14"),sQuery(id+"F0.wireOp",EDGE,"E18.10.15"),sQuery(id+"F0.wireOp",EDGE,"E18.10.16"),sQuery(id+"F0.wireOp",EDGE,"E18.11.5"),sQuery(id+"F0.wireOp",EDGE,"E18.11.6"),sQuery(id+"F0.wireOp",EDGE,"E18.11.7"),sQuery(id+"F0.wireOp",EDGE,"E18.11.8"),sQuery(id+"F0.wireOp",EDGE,"E18.11.10"),sQuery(id+"F0.wireOp",EDGE,"E18.11.11"),sQuery(id+"F0.wireOp",EDGE,"E18.11.13"),sQuery(id+"F0.wireOp",EDGE,"E18.11.14"),sQuery(id+"F0.wireOp",EDGE,"E18.11.15"),sQuery(id+"F0.wireOp",EDGE,"E18.11.16")])],"isStart":true});
            var sketch = newSketch(context, id + "F4", { "sketchPlane" : qUnion([Q0])});
            skCircle(sketch, "E20", {"center": v(0, 0) * mm, "radius": 4.45 * mm});
            skSolve(sketch);
        }
        {
            var Q0;
            Q0 = qSketchRegion(id + "F4", true);
            extrude(context, id + "F5", {"entities" : qUnion([Q0]), "operationType" : NewBodyOperationType.ADD, "depth" : 12.7 * mm});
        }
        {
            var Q0;
            Q0=makeQuery(id+"F5.opExtrude","CAP_FACE",FACE,{"disambiguationData":[OSD([sQuery(id+"F4.wireOp",EDGE,"E20")])],"isStart":false});
            var sketch = newSketch(context, id + "F6", { "sketchPlane" : qUnion([Q0])});
            skCircle(sketch, "E21", {"center": v(0, 0) * mm, "radius": 10.25 * mm});
            skSolve(sketch);
        }
        {
            var Q0;
            Q0 = qSketchRegion(id + "F6", true);
            extrude(context, id + "F7", {"entities" : qUnion([Q0]), "operationType" : NewBodyOperationType.ADD, "oppositeDirection" : true, "depth" : 4.76 * mm});
        }
        {
            var Q0;
            Q0=makeQuery(id+"F7.boolean.opBoolean","MERGE",FACE,{"derivedFrom":[makeQuery(id+"F5.opExtrude","CAP_FACE",FACE,{"disambiguationData":[OSD([sQuery(id+"F4.wireOp",EDGE,"E20")])],"isStart":false}),makeQuery(id+"F7.opExtrude","CAP_FACE",FACE,{"disambiguationData":[OSD([sQuery(id+"F6.wireOp",EDGE,"E21")])],"isStart":true})]});
            var sketch = newSketch(context, id + "F8", { "sketchPlane" : qUnion([Q0])});
            skCircle(sketch, "E22", {"center": v(0, 0) * mm, "radius": 5 * mm});
            skSolve(sketch);
        }
        {
            var Q0;
            Q0 = qSketchRegion(id + "F8", true);
            extrude(context, id + "F9", {"entities" : qUnion([Q0]), "operationType" : NewBodyOperationType.REMOVE, "oppositeDirection" : true, "depth" : 1 * mm});
        }
        {
            var Q0;
            Q0=makeQuery(id+"F7.boolean.opBoolean","MERGE",FACE,{"derivedFrom":[makeQuery(id+"F5.opExtrude","CAP_FACE",FACE,{"disambiguationData":[OSD([sQuery(id+"F4.wireOp",EDGE,"E20")])],"isStart":false}),makeQuery(id+"F7.opExtrude","CAP_FACE",FACE,{"disambiguationData":[OSD([sQuery(id+"F6.wireOp",EDGE,"E21")])],"isStart":true})]});
            var sketch = newSketch(context, id + "F10", { "sketchPlane" : qUnion([Q0])});
            skCircle(sketch, "E23", {"center": v(7.5, 0) * mm, "radius": 0.55 * mm});
            skCircle(sketch, "E24.1.0", {"center": v(0, 7.5) * mm, "radius": 0.55 * mm});
            skCircle(sketch, "E24.2.0", {"center": v(-7.5, 0) * mm, "radius": 0.55 * mm});
            skCircle(sketch, "E24.3.0", {"center": v(0, -7.5) * mm, "radius": 0.55 * mm});
            skPoint(sketch, "E24.center", {"position": v(0, 0) * mm});
            skSolve(sketch);
        }
        {
            var Q0;
            Q0 = qSketchRegion(id + "F10", true);
            var Q1;
            Q1=makeQuery(id+"F7.opExtrude","CAP_FACE",FACE,{"disambiguationData":[OSD([sQuery(id+"F6.wireOp",EDGE,"E21")])],"isStart":false});
            extrude(context, id + "F11", {"entities" : qUnion([Q0]), "operationType" : NewBodyOperationType.REMOVE, "endBound" : BoundingType.UP_TO_SURFACE, "oppositeDirection" : true, "endBoundEntityFace" : qUnion([Q1]), "depth" : 25.4 * mm});
        }
    });
